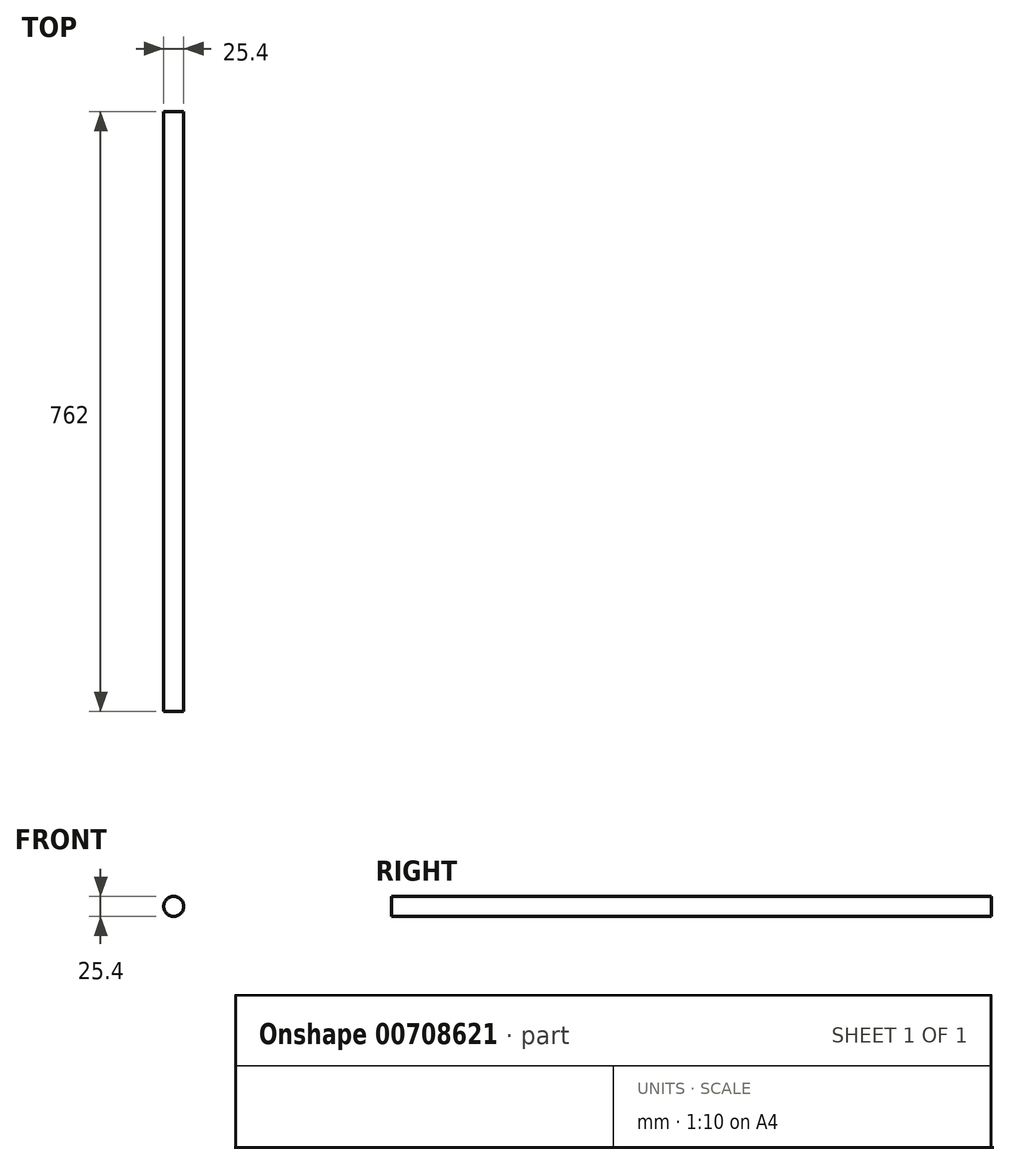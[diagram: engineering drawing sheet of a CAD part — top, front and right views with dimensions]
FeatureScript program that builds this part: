
annotation { "Feature Type Name" : "Feature", "Feature Type Description" : "" }
export const myFeature = defineFeature(function(context is Context, id is Id, definition is map)
    precondition{}
    {
        {
            var Q0;
            Q0=qCreatedBy(makeId("Front.planeOp"),FACE);
            var sketch = newSketch(context, id + "F0", { "sketchPlane" : qUnion([Q0])});
            skCircle(sketch, "E0", {"center": v(0, 0) * mm, "radius": 12.7 * mm});
            skSolve(sketch);
        }
        {
            var Q0;
            Q0 = qSketchRegion(id + "F0", true);
            extrude(context, id + "F1", {"entities" : qUnion([Q0]), "depth" : 762 * mm, "offsetDistance" : 25.4 * mm});
        }
    });
